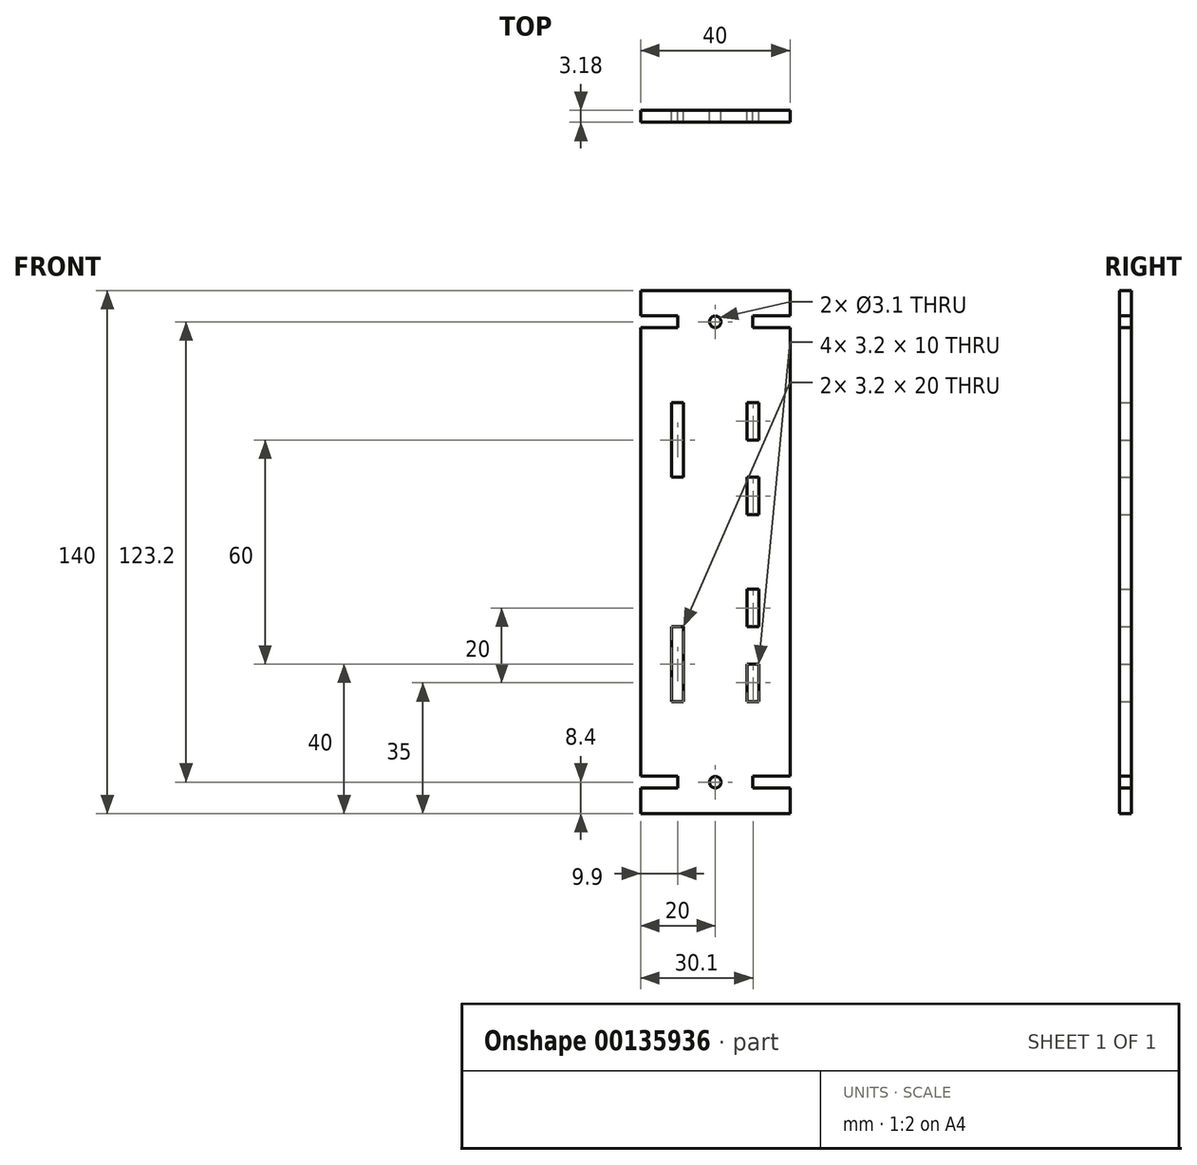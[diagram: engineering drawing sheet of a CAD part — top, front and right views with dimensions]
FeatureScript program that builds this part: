
annotation { "Feature Type Name" : "Feature", "Feature Type Description" : "" }
export const myFeature = defineFeature(function(context is Context, id is Id, definition is map)
    precondition{}
    {
        {
            var Q0;
            Q0=qCreatedBy(makeId("Front.planeOp"),FACE);
            var sketch = newSketch(context, id + "F0", { "sketchPlane" : qUnion([Q0])});
            skLineSegment(sketch, "E0", {"start": v(20, 0) * mm, "end": v(20, 60) * mm});
            skLineSegment(sketch, "E1", {"start": v(20, 60) * mm, "end": v(10, 60) * mm});
            skLineSegment(sketch, "E2", {"start": v(10, 60) * mm, "end": v(10, 63.2) * mm});
            skLineSegment(sketch, "E3", {"start": v(10, 63.2) * mm, "end": v(20, 63.2) * mm});
            skLineSegment(sketch, "E4", {"start": v(20, 63.2) * mm, "end": v(20, 70) * mm});
            skLineSegment(sketch, "E5", {"start": v(20, 70) * mm, "end": v(0, 70) * mm});
            skLineSegment(sketch, "E6.MirrorCS", {"start": v(-10, 60) * mm, "end": v(-10, 63.2) * mm});
            skLineSegment(sketch, "E7.MirrorCS", {"start": v(-20, 70) * mm, "end": v(0, 70) * mm});
            skLineSegment(sketch, "E8.MirrorCS", {"start": v(-20, 0) * mm, "end": v(-20, 60) * mm});
            skLineSegment(sketch, "E9.MirrorCS", {"start": v(-20, 63.2) * mm, "end": v(-20, 70) * mm});
            skLineSegment(sketch, "E10.MirrorCS", {"start": v(-20, 60) * mm, "end": v(-10, 60) * mm});
            skLineSegment(sketch, "E11.MirrorCS", {"start": v(-10, 63.2) * mm, "end": v(-20, 63.2) * mm});
            skLineSegment(sketch, "E12.MirrorCS", {"start": v(-10, -60) * mm, "end": v(-10, -63.2) * mm});
            skLineSegment(sketch, "E13.MirrorCS", {"start": v(10, -60) * mm, "end": v(10, -63.2) * mm});
            skLineSegment(sketch, "E14.MirrorCS", {"start": v(-10, -63.2) * mm, "end": v(-20, -63.2) * mm});
            skLineSegment(sketch, "E15.MirrorCS", {"start": v(-20, -60) * mm, "end": v(-10, -60) * mm});
            skLineSegment(sketch, "E16.MirrorCS", {"start": v(-20, -63.2) * mm, "end": v(-20, -70) * mm});
            skLineSegment(sketch, "E17.MirrorCS", {"start": v(-20, 0) * mm, "end": v(-20, -60) * mm});
            skLineSegment(sketch, "E18.MirrorCS", {"start": v(-20, -70) * mm, "end": v(0, -70) * mm});
            skLineSegment(sketch, "E19.MirrorCS", {"start": v(20, -70) * mm, "end": v(0, -70) * mm});
            skLineSegment(sketch, "E20.MirrorCS", {"start": v(10, -63.2) * mm, "end": v(20, -63.2) * mm});
            skLineSegment(sketch, "E21.MirrorCS", {"start": v(20, 0) * mm, "end": v(20, -60) * mm});
            skLineSegment(sketch, "E22.MirrorCS", {"start": v(20, -63.2) * mm, "end": v(20, -70) * mm});
            skLineSegment(sketch, "E23.MirrorCS", {"start": v(20, -60) * mm, "end": v(10, -60) * mm});
            skPoint(sketch, "E24", {"position": v(10, 61.6) * mm});
            skCircle(sketch, "E25", {"center": v(0, 61.6) * mm, "radius": 1.55 * mm});
            skCircle(sketch, "E26.MirrorC", {"center": v(0, -61.6) * mm, "radius": 1.55 * mm});
            skLineSegment(sketch, "E27.bottom", {"start": v(11.7, 10) * mm, "end": v(8.5, 10) * mm});
            skLineSegment(sketch, "E27.top", {"start": v(11.7, 20) * mm, "end": v(8.5, 20) * mm});
            skLineSegment(sketch, "E27.left", {"start": v(11.7, 10) * mm, "end": v(11.7, 20) * mm});
            skLineSegment(sketch, "E27.right", {"start": v(8.5, 10) * mm, "end": v(8.5, 20) * mm});
            skLineSegment(sketch, "E28.bottom", {"start": v(8.5, 30) * mm, "end": v(11.7, 30) * mm});
            skLineSegment(sketch, "E28.top", {"start": v(8.5, 40) * mm, "end": v(11.7, 40) * mm});
            skLineSegment(sketch, "E28.left", {"start": v(8.5, 30) * mm, "end": v(8.5, 40) * mm});
            skLineSegment(sketch, "E28.right", {"start": v(11.7, 30) * mm, "end": v(11.7, 40) * mm});
            skLineSegment(sketch, "E29.bottom", {"start": v(-8.5, 40) * mm, "end": v(-11.7, 40) * mm});
            skLineSegment(sketch, "E29.top", {"start": v(-8.5, 20) * mm, "end": v(-11.7, 20) * mm});
            skLineSegment(sketch, "E29.left", {"start": v(-8.5, 40) * mm, "end": v(-8.5, 20) * mm});
            skLineSegment(sketch, "E29.right", {"start": v(-11.7, 40) * mm, "end": v(-11.7, 20) * mm});
            skLineSegment(sketch, "E30.MirrorCS", {"start": v(-8.5, -40) * mm, "end": v(-11.7, -40) * mm});
            skLineSegment(sketch, "E31.MirrorCS", {"start": v(8.5, -40) * mm, "end": v(11.7, -40) * mm});
            skLineSegment(sketch, "E32.MirrorCS", {"start": v(11.7, -10) * mm, "end": v(8.5, -10) * mm});
            skLineSegment(sketch, "E33.MirrorCS", {"start": v(-8.5, -20) * mm, "end": v(-11.7, -20) * mm});
            skLineSegment(sketch, "E34.MirrorCS", {"start": v(8.5, -30) * mm, "end": v(11.7, -30) * mm});
            skLineSegment(sketch, "E35.MirrorCS", {"start": v(11.7, -20) * mm, "end": v(8.5, -20) * mm});
            skLineSegment(sketch, "E36.MirrorCS", {"start": v(8.5, -30) * mm, "end": v(8.5, -40) * mm});
            skLineSegment(sketch, "E37.MirrorCS", {"start": v(8.5, -10) * mm, "end": v(8.5, -20) * mm});
            skLineSegment(sketch, "E38.MirrorCS", {"start": v(-8.5, -40) * mm, "end": v(-8.5, -20) * mm});
            skLineSegment(sketch, "E39.MirrorCS", {"start": v(11.7, -10) * mm, "end": v(11.7, -20) * mm});
            skLineSegment(sketch, "E40.MirrorCS", {"start": v(11.7, -30) * mm, "end": v(11.7, -40) * mm});
            skLineSegment(sketch, "E41.MirrorCS", {"start": v(-11.7, -40) * mm, "end": v(-11.7, -20) * mm});
            skSolve(sketch);
        }
        {
            var Q0;
            Q0=makeQuery(id+"F0.imprint","IMPRINT",FACE,{"disambiguationData":[TD([[makeQuery(id+"F0.imprint","IMPRINT",EDGE,{"derivedFrom":sQuery(id+"F0.wireOp",EDGE,"E0")}),1.0]])]});
            extrude(context, id + "F1", {"entities" : qUnion([Q0]), "depth" : 3.17 * mm, "symmetric" : true});
        }
    });
